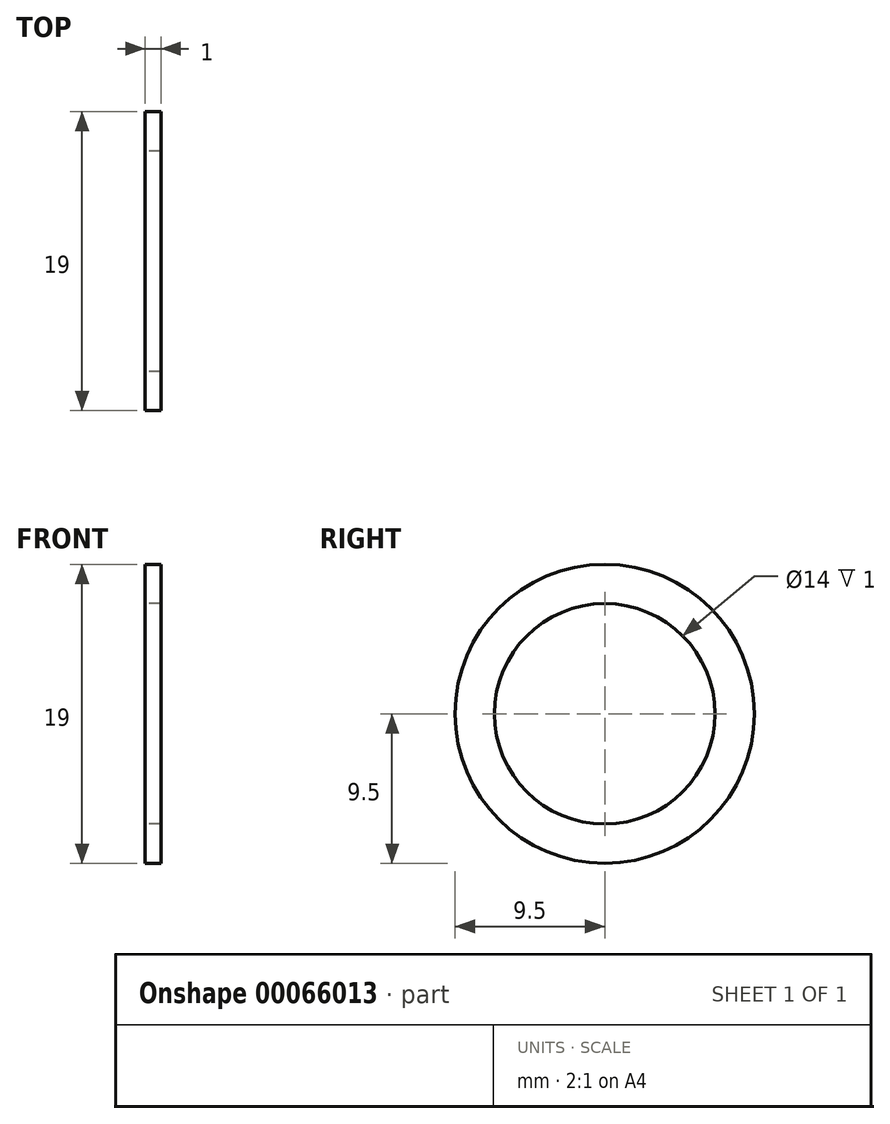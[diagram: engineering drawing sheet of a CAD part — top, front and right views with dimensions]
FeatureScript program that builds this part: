
annotation { "Feature Type Name" : "Feature", "Feature Type Description" : "" }
export const myFeature = defineFeature(function(context is Context, id is Id, definition is map)
    precondition{}
    {
        {
            var Q0;
            Q0=qCreatedBy(makeId("Right.planeOp"),FACE);
            var sketch = newSketch(context, id + "F0", { "sketchPlane" : qUnion([Q0])});
            skCircle(sketch, "E0", {"center": v(0, 0) * mm, "radius": 7 * mm});
            skCircle(sketch, "E1", {"center": v(0, 0) * mm, "radius": 9.5 * mm});
            skSolve(sketch);
        }
        {
            var Q0;
            Q0 = qSketchRegion(id + "F0", true);
            extrude(context, id + "F1", {"entities" : qUnion([Q0]), "depth" : 1 * mm});
        }
    });
